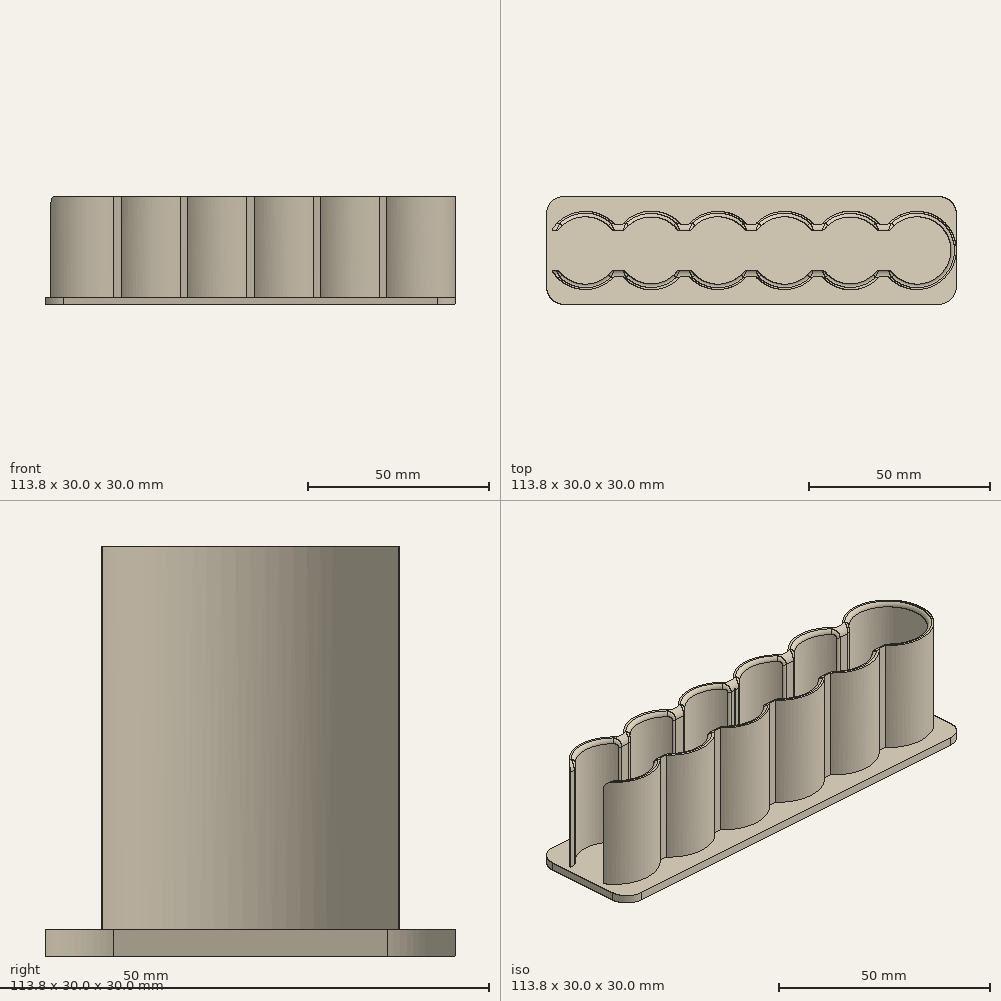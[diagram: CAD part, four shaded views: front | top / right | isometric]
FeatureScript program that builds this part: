
annotation { "Feature Type Name" : "Feature", "Feature Type Description" : "" }
export const myFeature = defineFeature(function(context is Context, id is Id, definition is map)
    precondition{}
    {
        {
            var Q0;
            Q0=qCreatedBy(makeId("Top.planeOp"),FACE);
            var sketch = newSketch(context, id + "F0", { "sketchPlane" : qUnion([Q0])});
            skArc(sketch, "E0", {"start": v(7.52, 5.55) * mm, "mid": v(-9.35, 0) * mm, "end": v(7.52, -5.55) * mm});
            skArc(sketch, "E1.2.0.0", {"start": v(29.28, -5.55) * mm, "mid": v(36.8, -9.35) * mm, "end": v(44.32, -5.55) * mm});
            skLineSegment(sketch, "E1.direction1", {"start": v(0, 0) * mm, "end": v(18.5, 0) * mm, "construction": true});
            skArc(sketch, "E2.0", {"start": v(8.15, 7.16) * mm, "mid": v(-10.85, 0) * mm, "end": v(8.15, -7.16) * mm});
            skArc(sketch, "E3.0", {"start": v(28.65, -7.16) * mm, "mid": v(36.8, -10.85) * mm, "end": v(44.95, -7.16) * mm});
            skLineSegment(sketch, "E4", {"start": v(8.15, 7.16) * mm, "end": v(10.25, 7.16) * mm});
            skLineSegment(sketch, "E5.1.0.0", {"start": v(26.55, 7.16) * mm, "end": v(28.65, 7.16) * mm});
            skLineSegment(sketch, "E5.direction1", {"start": v(8.15, 7.16) * mm, "end": v(10.25, 7.16) * mm, "construction": true});
            skLineSegment(sketch, "E6", {"start": v(9.2, 5.55) * mm, "end": v(7.52, 5.55) * mm});
            skLineSegment(sketch, "E7", {"start": v(7.52, 5.55) * mm, "end": v(10.88, 5.55) * mm});
            skLineSegment(sketch, "E8.MirrorCS", {"start": v(8.15, -7.16) * mm, "end": v(10.25, -7.16) * mm});
            skLineSegment(sketch, "E9.MirrorCS", {"start": v(7.52, -5.55) * mm, "end": v(10.88, -5.55) * mm});
            skLineSegment(sketch, "E10.MirrorCS", {"start": v(26.55, -7.16) * mm, "end": v(28.65, -7.16) * mm});
            skLineSegment(sketch, "E11.MirrorCS", {"start": v(25.68, -5.55) * mm, "end": v(29.28, -5.55) * mm});
            skArc(sketch, "E12.trimOffspring", {"start": v(10.25, -7.16) * mm, "mid": v(18.4, -10.93) * mm, "end": v(26.55, -7.16) * mm});
            skArc(sketch, "E13.trimOffspring", {"start": v(10.88, -5.55) * mm, "mid": v(18.28, -9.29) * mm, "end": v(25.68, -5.55) * mm});
            skArc(sketch, "E14.trimOffspring", {"start": v(26.55, 7.16) * mm, "mid": v(18.4, 10.93) * mm, "end": v(10.25, 7.16) * mm});
            skArc(sketch, "E15.trimOffspring", {"start": v(25.68, 5.55) * mm, "mid": v(18.28, 9.29) * mm, "end": v(10.88, 5.55) * mm});
            skLineSegment(sketch, "E16", {"start": v(25.68, 5.55) * mm, "end": v(29.28, 5.55) * mm});
            skArc(sketch, "E17", {"start": v(62.82, 5.55) * mm, "mid": v(55.3, 9.35) * mm, "end": v(47.78, 5.55) * mm});
            skArc(sketch, "E18.2.0.0", {"start": v(84.58, -5.55) * mm, "mid": v(101.45, 0) * mm, "end": v(84.58, 5.55) * mm});
            skLineSegment(sketch, "E18.direction1", {"start": v(55.3, 0) * mm, "end": v(73.8, 0) * mm, "construction": true});
            skArc(sketch, "E19.0", {"start": v(63.45, 7.16) * mm, "mid": v(55.3, 10.85) * mm, "end": v(47.15, 7.16) * mm});
            skArc(sketch, "E20.0", {"start": v(83.95, -7.16) * mm, "mid": v(102.95, 0) * mm, "end": v(83.95, 7.16) * mm});
            skLineSegment(sketch, "E21", {"start": v(63.45, 7.16) * mm, "end": v(65.55, 7.16) * mm});
            skLineSegment(sketch, "E22.1.0.0", {"start": v(81.85, 7.16) * mm, "end": v(83.95, 7.16) * mm});
            skLineSegment(sketch, "E22.direction1", {"start": v(63.45, 7.16) * mm, "end": v(65.55, 7.16) * mm, "construction": true});
            skLineSegment(sketch, "E23", {"start": v(64.5, 5.55) * mm, "end": v(62.82, 5.55) * mm});
            skLineSegment(sketch, "E24", {"start": v(62.82, 5.55) * mm, "end": v(66.18, 5.55) * mm});
            skLineSegment(sketch, "E25.MirrorCS", {"start": v(63.45, -7.16) * mm, "end": v(65.55, -7.16) * mm});
            skLineSegment(sketch, "E26.MirrorCS", {"start": v(62.82, -5.55) * mm, "end": v(66.18, -5.55) * mm});
            skLineSegment(sketch, "E27.MirrorCS", {"start": v(81.85, -7.16) * mm, "end": v(83.95, -7.16) * mm});
            skLineSegment(sketch, "E28.MirrorCS", {"start": v(80.98, -5.55) * mm, "end": v(84.58, -5.55) * mm});
            skArc(sketch, "E29.trimOffspring", {"start": v(65.55, -7.16) * mm, "mid": v(73.7, -10.93) * mm, "end": v(81.85, -7.16) * mm});
            skArc(sketch, "E30.trimOffspring", {"start": v(66.18, -5.55) * mm, "mid": v(73.58, -9.29) * mm, "end": v(80.98, -5.55) * mm});
            skArc(sketch, "E31.trimOffspring", {"start": v(81.85, 7.16) * mm, "mid": v(73.7, 10.93) * mm, "end": v(65.55, 7.16) * mm});
            skArc(sketch, "E32.trimOffspring", {"start": v(80.98, 5.55) * mm, "mid": v(73.58, 9.29) * mm, "end": v(66.18, 5.55) * mm});
            skLineSegment(sketch, "E33", {"start": v(80.98, 5.55) * mm, "end": v(84.58, 5.55) * mm});
            skLineSegment(sketch, "E34.0.3.0", {"start": v(63.35, 7.16) * mm, "end": v(65.45, 7.16) * mm});
            skLineSegment(sketch, "E35", {"start": v(44.95, 7.16) * mm, "end": v(47.15, 7.16) * mm});
            skLineSegment(sketch, "E36", {"start": v(44.95, -7.16) * mm, "end": v(47.15, -7.16) * mm});
            skLineSegment(sketch, "E37", {"start": v(44.32, -5.55) * mm, "end": v(47.78, -5.55) * mm});
            skLineSegment(sketch, "E38", {"start": v(44.32, 5.55) * mm, "end": v(47.78, 5.55) * mm});
            skPoint(sketch, "E38.startSnap0", {"position": v(27.48, 5.55) * mm});
            skArc(sketch, "E39.trimOffspring", {"start": v(44.95, 7.16) * mm, "mid": v(36.8, 10.85) * mm, "end": v(28.65, 7.16) * mm});
            skArc(sketch, "E40.trimOffspring", {"start": v(46.05, 5.67) * mm, "mid": v(46.01, 5.61) * mm, "end": v(45.98, 5.55) * mm});
            skArc(sketch, "E41.trimOffspring", {"start": v(46.12, 5.55) * mm, "mid": v(46.09, 5.61) * mm, "end": v(46.05, 5.67) * mm});
            skArc(sketch, "E42.trimOffspring", {"start": v(47.78, -5.55) * mm, "mid": v(55.3, -9.35) * mm, "end": v(62.82, -5.55) * mm});
            skArc(sketch, "E43.trimOffspring", {"start": v(44.32, 5.55) * mm, "mid": v(36.8, 9.35) * mm, "end": v(29.28, 5.55) * mm});
            skArc(sketch, "E44.trimOffspring", {"start": v(45.98, -5.55) * mm, "mid": v(46.01, -5.61) * mm, "end": v(46.05, -5.67) * mm});
            skArc(sketch, "E45.trimOffspring", {"start": v(46.05, -5.67) * mm, "mid": v(46.09, -5.61) * mm, "end": v(46.12, -5.55) * mm});
            skArc(sketch, "E46.trimOffspring", {"start": v(47.15, -7.16) * mm, "mid": v(55.3, -10.85) * mm, "end": v(63.45, -7.16) * mm});
            skSolve(sketch);
        }
        {
            var Q0;
            {var subQ3=sQuery(id+"F0.wireOp",EDGE,"E0");Q0=makeQuery(id+"F0.imprint","IMPRINT",FACE,{"disambiguationData":[TD([[makeQuery(id+"F0.imprint","IMPRINT",EDGE,{"derivedFrom":subQ3}),-1.0]])]});}
            extrude(context, id + "F1", {"entities" : qUnion([Q0]), "depth" : 30 * mm, "offsetDistance" : 25 * mm});
        }
        {
            var Q0;
            Q0=qCreatedBy(makeId("Top.planeOp"),FACE);
            var sketch = newSketch(context, id + "F2", { "sketchPlane" : qUnion([Q0])});
            skLineSegment(sketch, "E47.bottom", {"start": v(-10.85, -15) * mm, "end": v(103, -15) * mm});
            skLineSegment(sketch, "E47.top", {"start": v(-10.85, 15) * mm, "end": v(103, 15) * mm});
            skLineSegment(sketch, "E47.left", {"start": v(-10.85, -15) * mm, "end": v(-10.85, 15) * mm});
            skLineSegment(sketch, "E47.right", {"start": v(103, -15) * mm, "end": v(103, 15) * mm});
            skPoint(sketch, "E47.middle", {"position": v(46.07, 0) * mm});
            skSolve(sketch);
        }
        {
            var Q0;
            Q0=makeQuery(id+"F2.imprint","IMPRINT",FACE,{"disambiguationData":[TD([[makeQuery(id+"F2.imprint","IMPRINT",EDGE,{"derivedFrom":sQuery(id+"F2.wireOp",EDGE,"E47.bottom")}),1.0]])]});
            extrude(context, id + "F3", {"entities" : qUnion([Q0]), "operationType" : NewBodyOperationType.ADD, "depth" : 2 * mm});
        }
        {
            var Q0;
            Q0=makeQuery(id+"F3.opExtrude","SWEPT_EDGE",EDGE,{"disambiguationData":[OSD([sQuery(id+"F2.wireOp",EDGE,"E47.bottom"),sQuery(id+"F2.wireOp",EDGE,"E47.left")])]});
            var Q1;
            Q1=makeQuery(id+"F3.opExtrude","SWEPT_EDGE",EDGE,{"disambiguationData":[OSD([sQuery(id+"F2.wireOp",EDGE,"E47.bottom"),sQuery(id+"F2.wireOp",EDGE,"E47.right")])]});
            var Q2;
            Q2=makeQuery(id+"F3.opExtrude","SWEPT_EDGE",EDGE,{"disambiguationData":[OSD([sQuery(id+"F2.wireOp",EDGE,"E47.top"),sQuery(id+"F2.wireOp",EDGE,"E47.left")])]});
            var Q3;
            Q3=makeQuery(id+"F3.opExtrude","SWEPT_EDGE",EDGE,{"disambiguationData":[OSD([sQuery(id+"F2.wireOp",EDGE,"E47.top"),sQuery(id+"F2.wireOp",EDGE,"E47.right")])]});
            fillet(context, id + "F4", {"entities" : qUnion([Q0, Q1, Q2, Q3]), "radius" : 5 * mm, "tangentPropagation" : true, "allowEdgeOverflow" : false});
        }
        {
            var Q0;
            Q0=qCreatedBy(makeId("Right.planeOp"),FACE);
            var sketch = newSketch(context, id + "F5", { "sketchPlane" : qUnion([Q0])});
            skLineSegment(sketch, "E48.bottom", {"start": v(-5.5, 2) * mm, "end": v(5.5, 2) * mm});
            skLineSegment(sketch, "E48.top", {"start": v(-5.5, 52) * mm, "end": v(5.5, 52) * mm});
            skLineSegment(sketch, "E48.left", {"start": v(-5.5, 2) * mm, "end": v(-5.5, 52) * mm});
            skLineSegment(sketch, "E48.right", {"start": v(5.5, 2) * mm, "end": v(5.5, 52) * mm});
            skPoint(sketch, "E48.middle", {"position": v(0, 27) * mm});
            skSolve(sketch);
        }
        {
            var Q0;
            Q0=makeQuery(id+"F5.imprint","IMPRINT",FACE,{"disambiguationData":[TD([[makeQuery(id+"F5.imprint","IMPRINT",EDGE,{"derivedFrom":sQuery(id+"F5.wireOp",EDGE,"E48.bottom")}),1.0]])]});
            extrude(context, id + "F6", {"entities" : qUnion([Q0]), "operationType" : NewBodyOperationType.REMOVE, "oppositeDirection" : true, "depth" : 25 * mm});
        }
        {
            var Q0;
            Q0=makeQuery(id+"F1.opExtrude","CAP_EDGE",EDGE,{"disambiguationData":[OSD([sQuery(id+"F0.wireOp",EDGE,"E7")])],"isStart":false});
            var Q1;
            Q1=makeQuery(id+"F1.opExtrude","CAP_EDGE",EDGE,{"disambiguationData":[OSD([sQuery(id+"F0.wireOp",EDGE,"E16")])],"isStart":false});
            var Q2;
            {var subQ0=sQuery(id+"F0.wireOp",EDGE,"E38");Q2=makeQuery(id+"F1.opExtrude","CAP_EDGE",EDGE,{"disambiguationData":[OSD([subQ0]),TDD([makeQuery(id+"F0.imprint","IMPRINT",EDGE,{"disambiguationData":[TD([[makeQuery(id+"F0.imprint","INTERSECT",VERTEX,{"derivedFrom":[subQ0,sQuery(id+"F0.wireOp",EDGE,"E43.trimOffspring")]}),-1.0]])],"derivedFrom":subQ0})])],"isStart":false});}
            var Q3;
            Q3=makeQuery(id+"F1.opExtrude","CAP_EDGE",EDGE,{"disambiguationData":[OSD([sQuery(id+"F0.wireOp",EDGE,"E24")])],"isStart":false});
            var Q4;
            Q4=makeQuery(id+"F1.opExtrude","CAP_EDGE",EDGE,{"disambiguationData":[OSD([sQuery(id+"F0.wireOp",EDGE,"E33")])],"isStart":false});
            var Q5;
            Q5=makeQuery(id+"F1.opExtrude","CAP_EDGE",EDGE,{"disambiguationData":[OSD([sQuery(id+"F0.wireOp",EDGE,"E9.MirrorCS")])],"isStart":false});
            var Q6;
            Q6=makeQuery(id+"F1.opExtrude","CAP_EDGE",EDGE,{"disambiguationData":[OSD([sQuery(id+"F0.wireOp",EDGE,"E11.MirrorCS")])],"isStart":false});
            var Q7;
            {var subQ0=sQuery(id+"F0.wireOp",EDGE,"E37");Q7=makeQuery(id+"F1.opExtrude","CAP_EDGE",EDGE,{"disambiguationData":[OSD([subQ0]),TDD([makeQuery(id+"F0.imprint","IMPRINT",EDGE,{"disambiguationData":[TD([[makeQuery(id+"F0.imprint","INTERSECT",VERTEX,{"derivedFrom":[sQuery(id+"F0.wireOp",EDGE,"E1.2.0.0"),subQ0]}),-1.0]])],"derivedFrom":subQ0})])],"isStart":false});}
            var Q8;
            Q8=makeQuery(id+"F1.opExtrude","CAP_EDGE",EDGE,{"disambiguationData":[OSD([sQuery(id+"F0.wireOp",EDGE,"E26.MirrorCS")])],"isStart":false});
            var Q9;
            Q9=makeQuery(id+"F1.opExtrude","CAP_EDGE",EDGE,{"disambiguationData":[OSD([sQuery(id+"F0.wireOp",EDGE,"E28.MirrorCS")])],"isStart":false});
            var Q10;
            Q10=makeQuery(id+"F6.boolean.opBoolean","INTERSECT",EDGE,{"derivedFrom":[makeQuery(id+"F1.opExtrude","CAP_FACE",FACE,{"disambiguationData":[OSD([sQuery(id+"F0.wireOp",EDGE,"E0"),sQuery(id+"F0.wireOp",EDGE,"E1.2.0.0"),sQuery(id+"F0.wireOp",EDGE,"E2.0"),sQuery(id+"F0.wireOp",EDGE,"E3.0"),sQuery(id+"F0.wireOp",EDGE,"E4"),sQuery(id+"F0.wireOp",EDGE,"E5.1.0.0"),sQuery(id+"F0.wireOp",EDGE,"E7"),sQuery(id+"F0.wireOp",EDGE,"E8.MirrorCS"),sQuery(id+"F0.wireOp",EDGE,"E9.MirrorCS"),sQuery(id+"F0.wireOp",EDGE,"E10.MirrorCS"),sQuery(id+"F0.wireOp",EDGE,"E11.MirrorCS"),sQuery(id+"F0.wireOp",EDGE,"E12.trimOffspring"),sQuery(id+"F0.wireOp",EDGE,"E13.trimOffspring"),sQuery(id+"F0.wireOp",EDGE,"E14.trimOffspring"),sQuery(id+"F0.wireOp",EDGE,"E15.trimOffspring"),sQuery(id+"F0.wireOp",EDGE,"E16"),sQuery(id+"F0.wireOp",EDGE,"E17"),sQuery(id+"F0.wireOp",EDGE,"E18.2.0.0"),sQuery(id+"F0.wireOp",EDGE,"E19.0"),sQuery(id+"F0.wireOp",EDGE,"E20.0"),sQuery(id+"F0.wireOp",EDGE,"E21"),sQuery(id+"F0.wireOp",EDGE,"E22.1.0.0"),sQuery(id+"F0.wireOp",EDGE,"E24"),sQuery(id+"F0.wireOp",EDGE,"E25.MirrorCS"),sQuery(id+"F0.wireOp",EDGE,"E26.MirrorCS"),sQuery(id+"F0.wireOp",EDGE,"E27.MirrorCS"),sQuery(id+"F0.wireOp",EDGE,"E28.MirrorCS"),sQuery(id+"F0.wireOp",EDGE,"E29.trimOffspring"),sQuery(id+"F0.wireOp",EDGE,"E30.trimOffspring"),sQuery(id+"F0.wireOp",EDGE,"E31.trimOffspring"),sQuery(id+"F0.wireOp",EDGE,"E32.trimOffspring"),sQuery(id+"F0.wireOp",EDGE,"E33"),sQuery(id+"F0.wireOp",EDGE,"E34.0.3.0"),sQuery(id+"F0.wireOp",EDGE,"E35"),sQuery(id+"F0.wireOp",EDGE,"E36"),sQuery(id+"F0.wireOp",EDGE,"E37"),sQuery(id+"F0.wireOp",EDGE,"E38"),sQuery(id+"F0.wireOp",EDGE,"E39.trimOffspring"),sQuery(id+"F0.wireOp",EDGE,"E40.trimOffspring"),sQuery(id+"F0.wireOp",EDGE,"E41.trimOffspring"),sQuery(id+"F0.wireOp",EDGE,"E42.trimOffspring"),sQuery(id+"F0.wireOp",EDGE,"E43.trimOffspring"),sQuery(id+"F0.wireOp",EDGE,"E44.trimOffspring"),sQuery(id+"F0.wireOp",EDGE,"E45.trimOffspring"),sQuery(id+"F0.wireOp",EDGE,"E46.trimOffspring")])],"isStart":false}),makeQuery(id+"F6.opExtrude","SWEPT_FACE",FACE,{"disambiguationData":[OSD([sQuery(id+"F5.wireOp",EDGE,"E48.left")])]})]});
            var Q11;
            Q11=makeQuery(id+"F6.boolean.opBoolean","INTERSECT",EDGE,{"derivedFrom":[makeQuery(id+"F1.opExtrude","CAP_FACE",FACE,{"disambiguationData":[OSD([sQuery(id+"F0.wireOp",EDGE,"E0"),sQuery(id+"F0.wireOp",EDGE,"E1.2.0.0"),sQuery(id+"F0.wireOp",EDGE,"E2.0"),sQuery(id+"F0.wireOp",EDGE,"E3.0"),sQuery(id+"F0.wireOp",EDGE,"E4"),sQuery(id+"F0.wireOp",EDGE,"E5.1.0.0"),sQuery(id+"F0.wireOp",EDGE,"E7"),sQuery(id+"F0.wireOp",EDGE,"E8.MirrorCS"),sQuery(id+"F0.wireOp",EDGE,"E9.MirrorCS"),sQuery(id+"F0.wireOp",EDGE,"E10.MirrorCS"),sQuery(id+"F0.wireOp",EDGE,"E11.MirrorCS"),sQuery(id+"F0.wireOp",EDGE,"E12.trimOffspring"),sQuery(id+"F0.wireOp",EDGE,"E13.trimOffspring"),sQuery(id+"F0.wireOp",EDGE,"E14.trimOffspring"),sQuery(id+"F0.wireOp",EDGE,"E15.trimOffspring"),sQuery(id+"F0.wireOp",EDGE,"E16"),sQuery(id+"F0.wireOp",EDGE,"E17"),sQuery(id+"F0.wireOp",EDGE,"E18.2.0.0"),sQuery(id+"F0.wireOp",EDGE,"E19.0"),sQuery(id+"F0.wireOp",EDGE,"E20.0"),sQuery(id+"F0.wireOp",EDGE,"E21"),sQuery(id+"F0.wireOp",EDGE,"E22.1.0.0"),sQuery(id+"F0.wireOp",EDGE,"E24"),sQuery(id+"F0.wireOp",EDGE,"E25.MirrorCS"),sQuery(id+"F0.wireOp",EDGE,"E26.MirrorCS"),sQuery(id+"F0.wireOp",EDGE,"E27.MirrorCS"),sQuery(id+"F0.wireOp",EDGE,"E28.MirrorCS"),sQuery(id+"F0.wireOp",EDGE,"E29.trimOffspring"),sQuery(id+"F0.wireOp",EDGE,"E30.trimOffspring"),sQuery(id+"F0.wireOp",EDGE,"E31.trimOffspring"),sQuery(id+"F0.wireOp",EDGE,"E32.trimOffspring"),sQuery(id+"F0.wireOp",EDGE,"E33"),sQuery(id+"F0.wireOp",EDGE,"E34.0.3.0"),sQuery(id+"F0.wireOp",EDGE,"E35"),sQuery(id+"F0.wireOp",EDGE,"E36"),sQuery(id+"F0.wireOp",EDGE,"E37"),sQuery(id+"F0.wireOp",EDGE,"E38"),sQuery(id+"F0.wireOp",EDGE,"E39.trimOffspring"),sQuery(id+"F0.wireOp",EDGE,"E40.trimOffspring"),sQuery(id+"F0.wireOp",EDGE,"E41.trimOffspring"),sQuery(id+"F0.wireOp",EDGE,"E42.trimOffspring"),sQuery(id+"F0.wireOp",EDGE,"E43.trimOffspring"),sQuery(id+"F0.wireOp",EDGE,"E44.trimOffspring"),sQuery(id+"F0.wireOp",EDGE,"E45.trimOffspring"),sQuery(id+"F0.wireOp",EDGE,"E46.trimOffspring")])],"isStart":false}),makeQuery(id+"F6.opExtrude","SWEPT_FACE",FACE,{"disambiguationData":[OSD([sQuery(id+"F5.wireOp",EDGE,"E48.right")])]})]});
            fillet(context, id + "F7", {"entities" : qUnion([Q0, Q1, Q2, Q3, Q4, Q5, Q6, Q7, Q8, Q9, Q10, Q11]), "radius" : 2 * mm, "tangentPropagation" : true, "allowEdgeOverflow" : false});
        }
        {
            var Q0;
            {var subQ0=sQuery(id+"F0.wireOp",EDGE,"E0");var subQ1=sQuery(id+"F0.wireOp",EDGE,"E7");Q0=makeQuery(id+"F6.boolean.opBoolean","SPLIT",EDGE,{"disambiguationData":[TD([makeQuery(id+"F1.opExtrude","SWEPT_FACE",FACE,{"disambiguationData":[OSD([subQ1])]})])],"derivedFrom":makeQuery(id+"F1.opExtrude","CAP_EDGE",EDGE,{"disambiguationData":[OSD([subQ0])],"isStart":false})});}
            var Q1;
            Q1=makeQuery(id+"F1.opExtrude","CAP_EDGE",EDGE,{"disambiguationData":[OSD([sQuery(id+"F0.wireOp",EDGE,"E15.trimOffspring")])],"isStart":false});
            var Q2;
            Q2=makeQuery(id+"F1.opExtrude","CAP_EDGE",EDGE,{"disambiguationData":[OSD([sQuery(id+"F0.wireOp",EDGE,"E1.2.0.0")])],"isStart":false});
            var Q3;
            Q3=makeQuery(id+"F1.opExtrude","CAP_EDGE",EDGE,{"disambiguationData":[OSD([sQuery(id+"F0.wireOp",EDGE,"E13.trimOffspring")])],"isStart":false});
            var Q4;
            {var subQ0=sQuery(id+"F0.wireOp",EDGE,"E0");var subQ1=sQuery(id+"F0.wireOp",EDGE,"E9.MirrorCS");Q4=makeQuery(id+"F6.boolean.opBoolean","SPLIT",EDGE,{"disambiguationData":[TD([makeQuery(id+"F1.opExtrude","SWEPT_FACE",FACE,{"disambiguationData":[OSD([subQ1])]})])],"derivedFrom":makeQuery(id+"F1.opExtrude","CAP_EDGE",EDGE,{"disambiguationData":[OSD([subQ0])],"isStart":false})});}
            var Q5;
            Q5=makeQuery(id+"F1.opExtrude","CAP_EDGE",EDGE,{"disambiguationData":[OSD([sQuery(id+"F0.wireOp",EDGE,"E43.trimOffspring")])],"isStart":false});
            var Q6;
            Q6=makeQuery(id+"F1.opExtrude","CAP_EDGE",EDGE,{"disambiguationData":[OSD([sQuery(id+"F0.wireOp",EDGE,"E17")])],"isStart":false});
            var Q7;
            Q7=makeQuery(id+"F1.opExtrude","CAP_EDGE",EDGE,{"disambiguationData":[OSD([sQuery(id+"F0.wireOp",EDGE,"E32.trimOffspring")])],"isStart":false});
            var Q8;
            Q8=makeQuery(id+"F1.opExtrude","CAP_EDGE",EDGE,{"disambiguationData":[OSD([sQuery(id+"F0.wireOp",EDGE,"E18.2.0.0")])],"isStart":false});
            var Q9;
            Q9=makeQuery(id+"F1.opExtrude","CAP_EDGE",EDGE,{"disambiguationData":[OSD([sQuery(id+"F0.wireOp",EDGE,"E30.trimOffspring")])],"isStart":false});
            var Q10;
            Q10=makeQuery(id+"F1.opExtrude","CAP_EDGE",EDGE,{"disambiguationData":[OSD([sQuery(id+"F0.wireOp",EDGE,"E42.trimOffspring")])],"isStart":false});
            fillet(context, id + "F8", {"entities" : qUnion([Q0, Q1, Q2, Q3, Q4, Q5, Q6, Q7, Q8, Q9, Q10]), "radius" : 1 * mm, "tangentPropagation" : true, "allowEdgeOverflow" : false});
        }
    });
